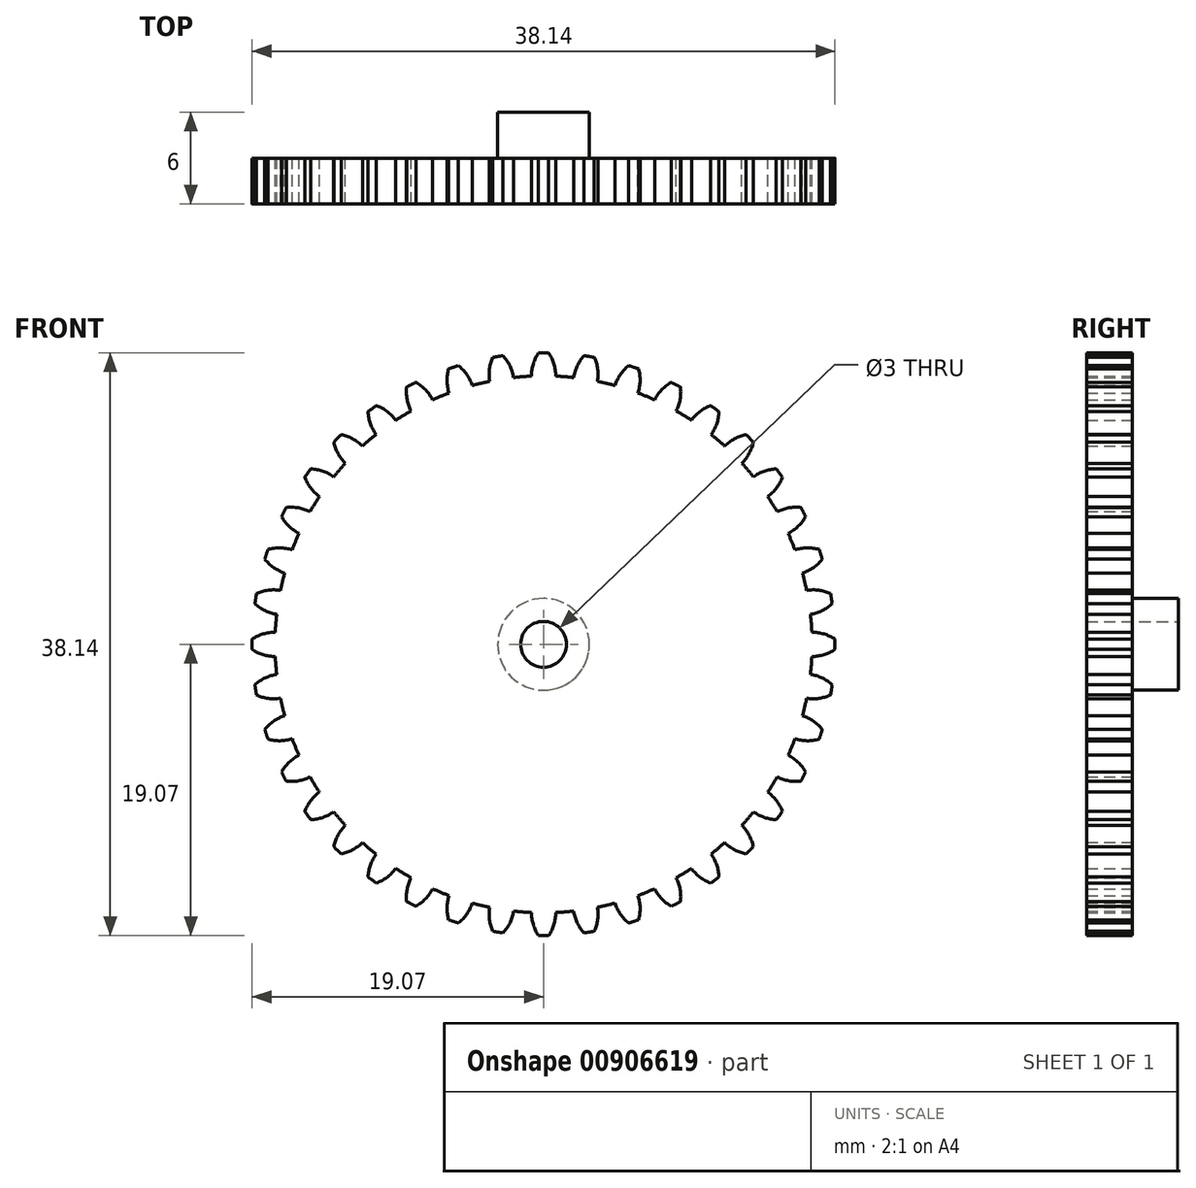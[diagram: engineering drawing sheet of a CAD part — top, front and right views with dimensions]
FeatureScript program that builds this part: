
annotation { "Feature Type Name" : "Feature", "Feature Type Description" : "" }
export const myFeature = defineFeature(function(context is Context, id is Id, definition is map)
    precondition{}
    {
        {
            var Q0;
            Q0=qCreatedBy(makeId("Front.planeOp"),FACE);
            var sketch = newSketch(context, id + "F0", { "sketchPlane" : qUnion([Q0])});
            skCircle(sketch, "E0", {"center": v(0, 0) * mm, "radius": 17.57 * mm});
            skArc(sketch, "E1", {"start": v(0.34, 19.07) * mm, "mid": v(0, 19.07) * mm, "end": v(-0.34, 19.07) * mm});
            skArc(sketch, "E2", {"start": v(-0.34, 19.07) * mm, "mid": v(-0.68, 18.34) * mm, "end": v(-0.8, 17.55) * mm});
            skArc(sketch, "E3.MirrorCS", {"start": v(0.34, 19.07) * mm, "mid": v(0.68, 18.34) * mm, "end": v(0.8, 17.55) * mm});
            skArc(sketch, "E4.1.0", {"start": v(-2.65, 18.89) * mm, "mid": v(-2.2, 18.22) * mm, "end": v(-1.96, 17.46) * mm});
            skArc(sketch, "E4.1.1", {"start": v(-2.65, 18.89) * mm, "mid": v(-2.98, 18.84) * mm, "end": v(-3.32, 18.78) * mm});
            skArc(sketch, "E4.1.2", {"start": v(-3.32, 18.78) * mm, "mid": v(-3.54, 18.01) * mm, "end": v(-3.53, 17.21) * mm});
            skArc(sketch, "E4.2.0", {"start": v(-5.57, 18.24) * mm, "mid": v(-5.02, 17.65) * mm, "end": v(-4.67, 16.94) * mm});
            skArc(sketch, "E4.2.1", {"start": v(-5.57, 18.24) * mm, "mid": v(-5.9, 18.14) * mm, "end": v(-6.21, 18.03) * mm});
            skArc(sketch, "E4.2.2", {"start": v(-6.21, 18.03) * mm, "mid": v(-6.31, 17.24) * mm, "end": v(-6.18, 16.45) * mm});
            skArc(sketch, "E4.3.0", {"start": v(-8.36, 17.14) * mm, "mid": v(-7.72, 16.65) * mm, "end": v(-7.26, 16) * mm});
            skArc(sketch, "E4.3.1", {"start": v(-8.36, 17.14) * mm, "mid": v(-8.66, 17) * mm, "end": v(-8.96, 16.84) * mm});
            skArc(sketch, "E4.3.2", {"start": v(-8.96, 16.84) * mm, "mid": v(-8.93, 16.04) * mm, "end": v(-8.68, 15.28) * mm});
            skArc(sketch, "E4.4.0", {"start": v(-10.93, 15.62) * mm, "mid": v(-10.23, 15.24) * mm, "end": v(-9.67, 14.67) * mm});
            skArc(sketch, "E4.4.1", {"start": v(-10.93, 15.62) * mm, "mid": v(-11.2, 15.43) * mm, "end": v(-11.48, 15.23) * mm});
            skArc(sketch, "E4.4.2", {"start": v(-11.48, 15.23) * mm, "mid": v(-11.33, 14.44) * mm, "end": v(-10.96, 13.73) * mm});
            skArc(sketch, "E4.5.0", {"start": v(-13.24, 13.72) * mm, "mid": v(-12.5, 13.45) * mm, "end": v(-11.85, 12.97) * mm});
            skArc(sketch, "E4.5.1", {"start": v(-13.24, 13.72) * mm, "mid": v(-13.48, 13.48) * mm, "end": v(-13.72, 13.24) * mm});
            skArc(sketch, "E4.5.2", {"start": v(-13.72, 13.24) * mm, "mid": v(-13.45, 12.5) * mm, "end": v(-12.97, 11.85) * mm});
            skArc(sketch, "E4.6.0", {"start": v(-15.23, 11.48) * mm, "mid": v(-14.44, 11.33) * mm, "end": v(-13.73, 10.96) * mm});
            skArc(sketch, "E4.6.1", {"start": v(-15.23, 11.48) * mm, "mid": v(-15.43, 11.2) * mm, "end": v(-15.62, 10.93) * mm});
            skArc(sketch, "E4.6.2", {"start": v(-15.62, 10.93) * mm, "mid": v(-15.24, 10.23) * mm, "end": v(-14.67, 9.67) * mm});
            skArc(sketch, "E4.7.0", {"start": v(-16.84, 8.96) * mm, "mid": v(-16.04, 8.93) * mm, "end": v(-15.28, 8.68) * mm});
            skArc(sketch, "E4.7.1", {"start": v(-16.84, 8.96) * mm, "mid": v(-17, 8.66) * mm, "end": v(-17.14, 8.36) * mm});
            skArc(sketch, "E4.7.2", {"start": v(-17.14, 8.36) * mm, "mid": v(-16.65, 7.72) * mm, "end": v(-16, 7.26) * mm});
            skArc(sketch, "E4.8.0", {"start": v(-18.03, 6.21) * mm, "mid": v(-17.24, 6.31) * mm, "end": v(-16.45, 6.18) * mm});
            skArc(sketch, "E4.8.1", {"start": v(-18.03, 6.21) * mm, "mid": v(-18.14, 5.9) * mm, "end": v(-18.24, 5.57) * mm});
            skArc(sketch, "E4.8.2", {"start": v(-18.24, 5.57) * mm, "mid": v(-17.65, 5.02) * mm, "end": v(-16.94, 4.67) * mm});
            skArc(sketch, "E5.1.9.0", {"start": v(-18.78, 3.32) * mm, "mid": v(-18.01, 3.54) * mm, "end": v(-17.21, 3.53) * mm});
            skArc(sketch, "E5.4.9.0", {"start": v(-18.78, 3.32) * mm, "mid": v(-18.84, 2.98) * mm, "end": v(-18.89, 2.65) * mm});
            skArc(sketch, "E5.8.9.0", {"start": v(-18.89, 2.65) * mm, "mid": v(-18.22, 2.2) * mm, "end": v(-17.46, 1.96) * mm});
            skArc(sketch, "E5.1.10.0", {"start": v(-19.07, 0.34) * mm, "mid": v(-18.34, 0.68) * mm, "end": v(-17.55, 0.8) * mm});
            skArc(sketch, "E5.4.10.0", {"start": v(-19.07, 0.34) * mm, "mid": v(-19.07, 0) * mm, "end": v(-19.07, -0.34) * mm});
            skArc(sketch, "E5.8.10.0", {"start": v(-19.07, -0.34) * mm, "mid": v(-18.34, -0.68) * mm, "end": v(-17.55, -0.8) * mm});
            skArc(sketch, "E5.1.11.0", {"start": v(-18.89, -2.65) * mm, "mid": v(-18.22, -2.2) * mm, "end": v(-17.46, -1.96) * mm});
            skArc(sketch, "E5.4.11.0", {"start": v(-18.89, -2.65) * mm, "mid": v(-18.84, -2.98) * mm, "end": v(-18.78, -3.32) * mm});
            skArc(sketch, "E5.8.11.0", {"start": v(-18.78, -3.32) * mm, "mid": v(-18.01, -3.54) * mm, "end": v(-17.21, -3.53) * mm});
            skArc(sketch, "E5.1.12.0", {"start": v(-18.24, -5.57) * mm, "mid": v(-17.65, -5.02) * mm, "end": v(-16.94, -4.67) * mm});
            skArc(sketch, "E5.4.12.0", {"start": v(-18.24, -5.57) * mm, "mid": v(-18.14, -5.9) * mm, "end": v(-18.03, -6.21) * mm});
            skArc(sketch, "E5.8.12.0", {"start": v(-18.03, -6.21) * mm, "mid": v(-17.24, -6.31) * mm, "end": v(-16.45, -6.18) * mm});
            skArc(sketch, "E5.1.13.0", {"start": v(-17.14, -8.36) * mm, "mid": v(-16.65, -7.72) * mm, "end": v(-16, -7.26) * mm});
            skArc(sketch, "E5.4.13.0", {"start": v(-17.14, -8.36) * mm, "mid": v(-17, -8.66) * mm, "end": v(-16.84, -8.96) * mm});
            skArc(sketch, "E5.8.13.0", {"start": v(-16.84, -8.96) * mm, "mid": v(-16.04, -8.93) * mm, "end": v(-15.28, -8.68) * mm});
            skArc(sketch, "E5.1.14.0", {"start": v(-15.62, -10.93) * mm, "mid": v(-15.24, -10.23) * mm, "end": v(-14.67, -9.67) * mm});
            skArc(sketch, "E5.4.14.0", {"start": v(-15.62, -10.93) * mm, "mid": v(-15.43, -11.2) * mm, "end": v(-15.23, -11.48) * mm});
            skArc(sketch, "E5.8.14.0", {"start": v(-15.23, -11.48) * mm, "mid": v(-14.44, -11.33) * mm, "end": v(-13.73, -10.96) * mm});
            skArc(sketch, "E5.1.15.0", {"start": v(-13.72, -13.24) * mm, "mid": v(-13.45, -12.5) * mm, "end": v(-12.97, -11.85) * mm});
            skArc(sketch, "E5.4.15.0", {"start": v(-13.72, -13.24) * mm, "mid": v(-13.48, -13.48) * mm, "end": v(-13.24, -13.72) * mm});
            skArc(sketch, "E5.8.15.0", {"start": v(-13.24, -13.72) * mm, "mid": v(-12.5, -13.45) * mm, "end": v(-11.85, -12.97) * mm});
            skArc(sketch, "E5.1.16.0", {"start": v(-11.48, -15.23) * mm, "mid": v(-11.33, -14.44) * mm, "end": v(-10.96, -13.73) * mm});
            skArc(sketch, "E5.4.16.0", {"start": v(-11.48, -15.23) * mm, "mid": v(-11.2, -15.43) * mm, "end": v(-10.93, -15.62) * mm});
            skArc(sketch, "E5.8.16.0", {"start": v(-10.93, -15.62) * mm, "mid": v(-10.23, -15.24) * mm, "end": v(-9.67, -14.67) * mm});
            skArc(sketch, "E5.1.17.0", {"start": v(-8.96, -16.84) * mm, "mid": v(-8.93, -16.04) * mm, "end": v(-8.68, -15.28) * mm});
            skArc(sketch, "E5.4.17.0", {"start": v(-8.96, -16.84) * mm, "mid": v(-8.66, -17) * mm, "end": v(-8.36, -17.14) * mm});
            skArc(sketch, "E5.8.17.0", {"start": v(-8.36, -17.14) * mm, "mid": v(-7.72, -16.65) * mm, "end": v(-7.26, -16) * mm});
            skArc(sketch, "E6.1.18.0", {"start": v(-6.21, -18.03) * mm, "mid": v(-6.31, -17.24) * mm, "end": v(-6.18, -16.45) * mm});
            skArc(sketch, "E6.4.18.0", {"start": v(-6.21, -18.03) * mm, "mid": v(-5.9, -18.14) * mm, "end": v(-5.57, -18.24) * mm});
            skArc(sketch, "E6.8.18.0", {"start": v(-5.57, -18.24) * mm, "mid": v(-5.02, -17.65) * mm, "end": v(-4.67, -16.94) * mm});
            skArc(sketch, "E7.1.19.0", {"start": v(-3.32, -18.78) * mm, "mid": v(-3.54, -18.01) * mm, "end": v(-3.53, -17.21) * mm});
            skArc(sketch, "E7.4.19.0", {"start": v(-3.32, -18.78) * mm, "mid": v(-2.98, -18.84) * mm, "end": v(-2.65, -18.89) * mm});
            skArc(sketch, "E7.8.19.0", {"start": v(-2.65, -18.89) * mm, "mid": v(-2.2, -18.22) * mm, "end": v(-1.96, -17.46) * mm});
            skArc(sketch, "E8.1.20.0", {"start": v(-0.34, -19.07) * mm, "mid": v(-0.68, -18.34) * mm, "end": v(-0.8, -17.55) * mm});
            skArc(sketch, "E8.4.20.0", {"start": v(-0.34, -19.07) * mm, "mid": v(0, -19.07) * mm, "end": v(0.34, -19.07) * mm});
            skArc(sketch, "E8.8.20.0", {"start": v(0.34, -19.07) * mm, "mid": v(0.68, -18.34) * mm, "end": v(0.8, -17.55) * mm});
            skArc(sketch, "E8.1.21.0", {"start": v(2.65, -18.89) * mm, "mid": v(2.2, -18.22) * mm, "end": v(1.96, -17.46) * mm});
            skArc(sketch, "E8.4.21.0", {"start": v(2.65, -18.89) * mm, "mid": v(2.98, -18.84) * mm, "end": v(3.32, -18.78) * mm});
            skArc(sketch, "E8.8.21.0", {"start": v(3.32, -18.78) * mm, "mid": v(3.54, -18.01) * mm, "end": v(3.53, -17.21) * mm});
            skArc(sketch, "E8.1.22.0", {"start": v(5.57, -18.24) * mm, "mid": v(5.02, -17.65) * mm, "end": v(4.67, -16.94) * mm});
            skArc(sketch, "E8.4.22.0", {"start": v(5.57, -18.24) * mm, "mid": v(5.9, -18.14) * mm, "end": v(6.21, -18.03) * mm});
            skArc(sketch, "E8.8.22.0", {"start": v(6.21, -18.03) * mm, "mid": v(6.31, -17.24) * mm, "end": v(6.18, -16.45) * mm});
            skArc(sketch, "E8.1.23.0", {"start": v(8.36, -17.14) * mm, "mid": v(7.72, -16.65) * mm, "end": v(7.26, -16) * mm});
            skArc(sketch, "E8.4.23.0", {"start": v(8.36, -17.14) * mm, "mid": v(8.66, -17) * mm, "end": v(8.96, -16.84) * mm});
            skArc(sketch, "E8.8.23.0", {"start": v(8.96, -16.84) * mm, "mid": v(8.93, -16.04) * mm, "end": v(8.68, -15.28) * mm});
            skArc(sketch, "E8.1.24.0", {"start": v(10.93, -15.62) * mm, "mid": v(10.23, -15.24) * mm, "end": v(9.67, -14.67) * mm});
            skArc(sketch, "E8.4.24.0", {"start": v(10.93, -15.62) * mm, "mid": v(11.2, -15.43) * mm, "end": v(11.48, -15.23) * mm});
            skArc(sketch, "E8.8.24.0", {"start": v(11.48, -15.23) * mm, "mid": v(11.33, -14.44) * mm, "end": v(10.96, -13.73) * mm});
            skArc(sketch, "E8.1.25.0", {"start": v(13.24, -13.72) * mm, "mid": v(12.5, -13.45) * mm, "end": v(11.85, -12.97) * mm});
            skArc(sketch, "E8.4.25.0", {"start": v(13.24, -13.72) * mm, "mid": v(13.48, -13.48) * mm, "end": v(13.72, -13.24) * mm});
            skArc(sketch, "E8.8.25.0", {"start": v(13.72, -13.24) * mm, "mid": v(13.45, -12.5) * mm, "end": v(12.97, -11.85) * mm});
            skArc(sketch, "E8.1.26.0", {"start": v(15.23, -11.48) * mm, "mid": v(14.44, -11.33) * mm, "end": v(13.73, -10.96) * mm});
            skArc(sketch, "E8.4.26.0", {"start": v(15.23, -11.48) * mm, "mid": v(15.43, -11.2) * mm, "end": v(15.62, -10.93) * mm});
            skArc(sketch, "E8.8.26.0", {"start": v(15.62, -10.93) * mm, "mid": v(15.24, -10.23) * mm, "end": v(14.67, -9.67) * mm});
            skArc(sketch, "E8.1.27.0", {"start": v(16.84, -8.96) * mm, "mid": v(16.04, -8.93) * mm, "end": v(15.28, -8.68) * mm});
            skArc(sketch, "E8.4.27.0", {"start": v(16.84, -8.96) * mm, "mid": v(17, -8.66) * mm, "end": v(17.14, -8.36) * mm});
            skArc(sketch, "E8.8.27.0", {"start": v(17.14, -8.36) * mm, "mid": v(16.65, -7.72) * mm, "end": v(16, -7.26) * mm});
            skArc(sketch, "E8.1.28.0", {"start": v(18.03, -6.21) * mm, "mid": v(17.24, -6.31) * mm, "end": v(16.45, -6.18) * mm});
            skArc(sketch, "E8.4.28.0", {"start": v(18.03, -6.21) * mm, "mid": v(18.14, -5.9) * mm, "end": v(18.24, -5.57) * mm});
            skArc(sketch, "E8.8.28.0", {"start": v(18.24, -5.57) * mm, "mid": v(17.65, -5.02) * mm, "end": v(16.94, -4.67) * mm});
            skArc(sketch, "E8.1.29.0", {"start": v(18.78, -3.32) * mm, "mid": v(18.01, -3.54) * mm, "end": v(17.21, -3.53) * mm});
            skArc(sketch, "E8.4.29.0", {"start": v(18.78, -3.32) * mm, "mid": v(18.84, -2.98) * mm, "end": v(18.89, -2.65) * mm});
            skArc(sketch, "E8.8.29.0", {"start": v(18.89, -2.65) * mm, "mid": v(18.22, -2.2) * mm, "end": v(17.46, -1.96) * mm});
            skArc(sketch, "E9.1.30.0", {"start": v(19.07, -0.34) * mm, "mid": v(18.34, -0.68) * mm, "end": v(17.55, -0.8) * mm});
            skArc(sketch, "E9.4.30.0", {"start": v(19.07, -0.34) * mm, "mid": v(19.07, 0) * mm, "end": v(19.07, 0.34) * mm});
            skArc(sketch, "E9.8.30.0", {"start": v(19.07, 0.34) * mm, "mid": v(18.34, 0.68) * mm, "end": v(17.55, 0.8) * mm});
            skArc(sketch, "E9.1.31.0", {"start": v(18.89, 2.65) * mm, "mid": v(18.22, 2.2) * mm, "end": v(17.46, 1.96) * mm});
            skArc(sketch, "E9.4.31.0", {"start": v(18.89, 2.65) * mm, "mid": v(18.84, 2.98) * mm, "end": v(18.78, 3.32) * mm});
            skArc(sketch, "E9.8.31.0", {"start": v(18.78, 3.32) * mm, "mid": v(18.01, 3.54) * mm, "end": v(17.21, 3.53) * mm});
            skArc(sketch, "E9.1.32.0", {"start": v(18.24, 5.57) * mm, "mid": v(17.65, 5.02) * mm, "end": v(16.94, 4.67) * mm});
            skArc(sketch, "E9.4.32.0", {"start": v(18.24, 5.57) * mm, "mid": v(18.14, 5.9) * mm, "end": v(18.03, 6.21) * mm});
            skArc(sketch, "E9.8.32.0", {"start": v(18.03, 6.21) * mm, "mid": v(17.24, 6.31) * mm, "end": v(16.45, 6.18) * mm});
            skArc(sketch, "E9.1.33.0", {"start": v(17.14, 8.36) * mm, "mid": v(16.65, 7.72) * mm, "end": v(16, 7.26) * mm});
            skArc(sketch, "E9.4.33.0", {"start": v(17.14, 8.36) * mm, "mid": v(17, 8.66) * mm, "end": v(16.84, 8.96) * mm});
            skArc(sketch, "E9.8.33.0", {"start": v(16.84, 8.96) * mm, "mid": v(16.04, 8.93) * mm, "end": v(15.28, 8.68) * mm});
            skArc(sketch, "E9.1.34.0", {"start": v(15.62, 10.93) * mm, "mid": v(15.24, 10.23) * mm, "end": v(14.67, 9.67) * mm});
            skArc(sketch, "E9.4.34.0", {"start": v(15.62, 10.93) * mm, "mid": v(15.43, 11.2) * mm, "end": v(15.23, 11.48) * mm});
            skArc(sketch, "E9.8.34.0", {"start": v(15.23, 11.48) * mm, "mid": v(14.44, 11.33) * mm, "end": v(13.73, 10.96) * mm});
            skArc(sketch, "E9.1.35.0", {"start": v(13.72, 13.24) * mm, "mid": v(13.45, 12.5) * mm, "end": v(12.97, 11.85) * mm});
            skArc(sketch, "E9.4.35.0", {"start": v(13.72, 13.24) * mm, "mid": v(13.48, 13.48) * mm, "end": v(13.24, 13.72) * mm});
            skArc(sketch, "E9.8.35.0", {"start": v(13.24, 13.72) * mm, "mid": v(12.5, 13.45) * mm, "end": v(11.85, 12.97) * mm});
            skArc(sketch, "E9.1.36.0", {"start": v(11.48, 15.23) * mm, "mid": v(11.33, 14.44) * mm, "end": v(10.96, 13.73) * mm});
            skArc(sketch, "E9.4.36.0", {"start": v(11.48, 15.23) * mm, "mid": v(11.2, 15.43) * mm, "end": v(10.93, 15.62) * mm});
            skArc(sketch, "E9.8.36.0", {"start": v(10.93, 15.62) * mm, "mid": v(10.23, 15.24) * mm, "end": v(9.67, 14.67) * mm});
            skArc(sketch, "E9.1.37.0", {"start": v(8.96, 16.84) * mm, "mid": v(8.93, 16.04) * mm, "end": v(8.68, 15.28) * mm});
            skArc(sketch, "E9.4.37.0", {"start": v(8.96, 16.84) * mm, "mid": v(8.66, 17) * mm, "end": v(8.36, 17.14) * mm});
            skArc(sketch, "E9.8.37.0", {"start": v(8.36, 17.14) * mm, "mid": v(7.72, 16.65) * mm, "end": v(7.26, 16) * mm});
            skArc(sketch, "E9.1.38.0", {"start": v(6.21, 18.03) * mm, "mid": v(6.31, 17.24) * mm, "end": v(6.18, 16.45) * mm});
            skArc(sketch, "E9.4.38.0", {"start": v(6.21, 18.03) * mm, "mid": v(5.9, 18.14) * mm, "end": v(5.57, 18.24) * mm});
            skArc(sketch, "E9.8.38.0", {"start": v(5.57, 18.24) * mm, "mid": v(5.02, 17.65) * mm, "end": v(4.67, 16.94) * mm});
            skArc(sketch, "E9.1.39.0", {"start": v(3.32, 18.78) * mm, "mid": v(3.54, 18.01) * mm, "end": v(3.53, 17.21) * mm});
            skArc(sketch, "E9.4.39.0", {"start": v(3.32, 18.78) * mm, "mid": v(2.98, 18.84) * mm, "end": v(2.65, 18.89) * mm});
            skArc(sketch, "E9.8.39.0", {"start": v(2.65, 18.89) * mm, "mid": v(2.2, 18.22) * mm, "end": v(1.96, 17.46) * mm});
            skSolve(sketch);
        }
        {
            var Q0;
            Q0=qSketchRegion(id+"F0",true);
            extrude(context, id + "F1", {"entities" : qUnion([Q0]), "depth" : 3 * mm, "offsetDistance" : 25 * mm});
        }
        {
            var Q0;
            Q0=makeQuery(id+"F1.opExtrude","CAP_FACE",FACE,{"disambiguationData":[OSD([sQuery(id+"F0.wireOp",EDGE,"E0"),sQuery(id+"F0.wireOp",EDGE,"E1"),sQuery(id+"F0.wireOp",EDGE,"E2"),sQuery(id+"F0.wireOp",EDGE,"E3.MirrorCS"),sQuery(id+"F0.wireOp",EDGE,"E4.1.0"),sQuery(id+"F0.wireOp",EDGE,"E4.1.1"),sQuery(id+"F0.wireOp",EDGE,"E4.1.2"),sQuery(id+"F0.wireOp",EDGE,"E4.2.0"),sQuery(id+"F0.wireOp",EDGE,"E4.2.1"),sQuery(id+"F0.wireOp",EDGE,"E4.2.2"),sQuery(id+"F0.wireOp",EDGE,"E4.3.0"),sQuery(id+"F0.wireOp",EDGE,"E4.3.1"),sQuery(id+"F0.wireOp",EDGE,"E4.3.2"),sQuery(id+"F0.wireOp",EDGE,"E4.4.0"),sQuery(id+"F0.wireOp",EDGE,"E4.4.1"),sQuery(id+"F0.wireOp",EDGE,"E4.4.2"),sQuery(id+"F0.wireOp",EDGE,"E4.5.0"),sQuery(id+"F0.wireOp",EDGE,"E4.5.1"),sQuery(id+"F0.wireOp",EDGE,"E4.5.2"),sQuery(id+"F0.wireOp",EDGE,"E4.6.0"),sQuery(id+"F0.wireOp",EDGE,"E4.6.1"),sQuery(id+"F0.wireOp",EDGE,"E4.6.2"),sQuery(id+"F0.wireOp",EDGE,"E4.7.0"),sQuery(id+"F0.wireOp",EDGE,"E4.7.1"),sQuery(id+"F0.wireOp",EDGE,"E4.7.2"),sQuery(id+"F0.wireOp",EDGE,"E4.8.0"),sQuery(id+"F0.wireOp",EDGE,"E4.8.1"),sQuery(id+"F0.wireOp",EDGE,"E4.8.2")])],"isStart":true});
            var sketch = newSketch(context, id + "F2", { "sketchPlane" : qUnion([Q0])});
            skCircle(sketch, "E10", {"center": v(0, 0) * mm, "radius": 1.5 * mm});
            skSolve(sketch);
        }
        {
            var Q0;
            Q0=makeQuery(id+"F2.imprint","IMPRINT",FACE,{"disambiguationData":[TD([[makeQuery(id+"F2.imprint","IMPRINT",EDGE,{"derivedFrom":sQuery(id+"F2.wireOp",EDGE,"E10")}),1.0]])]});
            extrude(context, id + "F3", {"entities" : qUnion([Q0]), "operationType" : NewBodyOperationType.REMOVE, "endBound" : BoundingType.THROUGH_ALL, "oppositeDirection" : true, "depth" : 25 * mm, "offsetDistance" : 25 * mm});
        }
        {
            var Q0;
            Q0=makeQuery(id+"F1.opExtrude","CAP_FACE",FACE,{"disambiguationData":[OSD([sQuery(id+"F0.wireOp",EDGE,"E0"),sQuery(id+"F0.wireOp",EDGE,"E1"),sQuery(id+"F0.wireOp",EDGE,"E2"),sQuery(id+"F0.wireOp",EDGE,"E3.MirrorCS"),sQuery(id+"F0.wireOp",EDGE,"E4.1.0"),sQuery(id+"F0.wireOp",EDGE,"E4.1.1"),sQuery(id+"F0.wireOp",EDGE,"E4.1.2"),sQuery(id+"F0.wireOp",EDGE,"E4.2.0"),sQuery(id+"F0.wireOp",EDGE,"E4.2.1"),sQuery(id+"F0.wireOp",EDGE,"E4.2.2"),sQuery(id+"F0.wireOp",EDGE,"E4.3.0"),sQuery(id+"F0.wireOp",EDGE,"E4.3.1"),sQuery(id+"F0.wireOp",EDGE,"E4.3.2"),sQuery(id+"F0.wireOp",EDGE,"E4.4.0"),sQuery(id+"F0.wireOp",EDGE,"E4.4.1"),sQuery(id+"F0.wireOp",EDGE,"E4.4.2"),sQuery(id+"F0.wireOp",EDGE,"E4.5.0"),sQuery(id+"F0.wireOp",EDGE,"E4.5.1"),sQuery(id+"F0.wireOp",EDGE,"E4.5.2"),sQuery(id+"F0.wireOp",EDGE,"E4.6.0"),sQuery(id+"F0.wireOp",EDGE,"E4.6.1"),sQuery(id+"F0.wireOp",EDGE,"E4.6.2"),sQuery(id+"F0.wireOp",EDGE,"E4.7.0"),sQuery(id+"F0.wireOp",EDGE,"E4.7.1"),sQuery(id+"F0.wireOp",EDGE,"E4.7.2"),sQuery(id+"F0.wireOp",EDGE,"E4.8.0"),sQuery(id+"F0.wireOp",EDGE,"E4.8.1"),sQuery(id+"F0.wireOp",EDGE,"E4.8.2"),sQuery(id+"F0.wireOp",EDGE,"E5.1.9.0"),sQuery(id+"F0.wireOp",EDGE,"E5.4.9.0"),sQuery(id+"F0.wireOp",EDGE,"E5.8.9.0"),sQuery(id+"F0.wireOp",EDGE,"E5.1.10.0"),sQuery(id+"F0.wireOp",EDGE,"E5.4.10.0"),sQuery(id+"F0.wireOp",EDGE,"E5.8.10.0"),sQuery(id+"F0.wireOp",EDGE,"E5.1.11.0"),sQuery(id+"F0.wireOp",EDGE,"E5.4.11.0"),sQuery(id+"F0.wireOp",EDGE,"E5.8.11.0"),sQuery(id+"F0.wireOp",EDGE,"E5.1.12.0"),sQuery(id+"F0.wireOp",EDGE,"E5.4.12.0"),sQuery(id+"F0.wireOp",EDGE,"E5.8.12.0"),sQuery(id+"F0.wireOp",EDGE,"E5.1.13.0"),sQuery(id+"F0.wireOp",EDGE,"E5.4.13.0"),sQuery(id+"F0.wireOp",EDGE,"E5.8.13.0"),sQuery(id+"F0.wireOp",EDGE,"E5.1.14.0"),sQuery(id+"F0.wireOp",EDGE,"E5.4.14.0"),sQuery(id+"F0.wireOp",EDGE,"E5.8.14.0"),sQuery(id+"F0.wireOp",EDGE,"E5.1.15.0"),sQuery(id+"F0.wireOp",EDGE,"E5.4.15.0"),sQuery(id+"F0.wireOp",EDGE,"E5.8.15.0"),sQuery(id+"F0.wireOp",EDGE,"E5.1.16.0"),sQuery(id+"F0.wireOp",EDGE,"E5.4.16.0"),sQuery(id+"F0.wireOp",EDGE,"E5.8.16.0"),sQuery(id+"F0.wireOp",EDGE,"E5.1.17.0"),sQuery(id+"F0.wireOp",EDGE,"E5.4.17.0"),sQuery(id+"F0.wireOp",EDGE,"E5.8.17.0"),sQuery(id+"F0.wireOp",EDGE,"E6.1.18.0"),sQuery(id+"F0.wireOp",EDGE,"E6.4.18.0"),sQuery(id+"F0.wireOp",EDGE,"E6.8.18.0"),sQuery(id+"F0.wireOp",EDGE,"E7.1.19.0"),sQuery(id+"F0.wireOp",EDGE,"E7.4.19.0"),sQuery(id+"F0.wireOp",EDGE,"E7.8.19.0"),sQuery(id+"F0.wireOp",EDGE,"E8.1.20.0"),sQuery(id+"F0.wireOp",EDGE,"E8.4.20.0"),sQuery(id+"F0.wireOp",EDGE,"E8.8.20.0"),sQuery(id+"F0.wireOp",EDGE,"E8.1.21.0"),sQuery(id+"F0.wireOp",EDGE,"E8.4.21.0"),sQuery(id+"F0.wireOp",EDGE,"E8.8.21.0"),sQuery(id+"F0.wireOp",EDGE,"E8.1.22.0"),sQuery(id+"F0.wireOp",EDGE,"E8.4.22.0"),sQuery(id+"F0.wireOp",EDGE,"E8.8.22.0"),sQuery(id+"F0.wireOp",EDGE,"E8.1.23.0"),sQuery(id+"F0.wireOp",EDGE,"E8.4.23.0"),sQuery(id+"F0.wireOp",EDGE,"E8.8.23.0"),sQuery(id+"F0.wireOp",EDGE,"E8.1.24.0"),sQuery(id+"F0.wireOp",EDGE,"E8.4.24.0"),sQuery(id+"F0.wireOp",EDGE,"E8.8.24.0"),sQuery(id+"F0.wireOp",EDGE,"E8.1.25.0"),sQuery(id+"F0.wireOp",EDGE,"E8.4.25.0"),sQuery(id+"F0.wireOp",EDGE,"E8.8.25.0"),sQuery(id+"F0.wireOp",EDGE,"E8.1.26.0"),sQuery(id+"F0.wireOp",EDGE,"E8.4.26.0"),sQuery(id+"F0.wireOp",EDGE,"E8.8.26.0"),sQuery(id+"F0.wireOp",EDGE,"E8.1.27.0"),sQuery(id+"F0.wireOp",EDGE,"E8.4.27.0"),sQuery(id+"F0.wireOp",EDGE,"E8.8.27.0"),sQuery(id+"F0.wireOp",EDGE,"E8.1.28.0"),sQuery(id+"F0.wireOp",EDGE,"E8.4.28.0"),sQuery(id+"F0.wireOp",EDGE,"E8.8.28.0"),sQuery(id+"F0.wireOp",EDGE,"E8.1.29.0"),sQuery(id+"F0.wireOp",EDGE,"E8.4.29.0"),sQuery(id+"F0.wireOp",EDGE,"E8.8.29.0"),sQuery(id+"F0.wireOp",EDGE,"E9.1.30.0"),sQuery(id+"F0.wireOp",EDGE,"E9.4.30.0"),sQuery(id+"F0.wireOp",EDGE,"E9.8.30.0"),sQuery(id+"F0.wireOp",EDGE,"E9.1.31.0"),sQuery(id+"F0.wireOp",EDGE,"E9.4.31.0"),sQuery(id+"F0.wireOp",EDGE,"E9.8.31.0"),sQuery(id+"F0.wireOp",EDGE,"E9.1.32.0"),sQuery(id+"F0.wireOp",EDGE,"E9.4.32.0"),sQuery(id+"F0.wireOp",EDGE,"E9.8.32.0"),sQuery(id+"F0.wireOp",EDGE,"E9.1.33.0"),sQuery(id+"F0.wireOp",EDGE,"E9.4.33.0"),sQuery(id+"F0.wireOp",EDGE,"E9.8.33.0"),sQuery(id+"F0.wireOp",EDGE,"E9.1.34.0"),sQuery(id+"F0.wireOp",EDGE,"E9.4.34.0"),sQuery(id+"F0.wireOp",EDGE,"E9.8.34.0"),sQuery(id+"F0.wireOp",EDGE,"E9.1.35.0"),sQuery(id+"F0.wireOp",EDGE,"E9.4.35.0"),sQuery(id+"F0.wireOp",EDGE,"E9.8.35.0"),sQuery(id+"F0.wireOp",EDGE,"E9.1.36.0"),sQuery(id+"F0.wireOp",EDGE,"E9.4.36.0"),sQuery(id+"F0.wireOp",EDGE,"E9.8.36.0"),sQuery(id+"F0.wireOp",EDGE,"E9.1.37.0"),sQuery(id+"F0.wireOp",EDGE,"E9.4.37.0"),sQuery(id+"F0.wireOp",EDGE,"E9.8.37.0"),sQuery(id+"F0.wireOp",EDGE,"E9.1.38.0"),sQuery(id+"F0.wireOp",EDGE,"E9.4.38.0"),sQuery(id+"F0.wireOp",EDGE,"E9.8.38.0"),sQuery(id+"F0.wireOp",EDGE,"E9.1.39.0"),sQuery(id+"F0.wireOp",EDGE,"E9.4.39.0"),sQuery(id+"F0.wireOp",EDGE,"E9.8.39.0")])],"isStart":true});
            var sketch = newSketch(context, id + "F4", { "sketchPlane" : qUnion([Q0])});
            skCircle(sketch, "E11", {"center": v(0, 0) * mm, "radius": 3 * mm});
            skCircle(sketch, "E12.0", {"center": v(0, 0) * mm, "radius": 1.5 * mm});
            skSolve(sketch);
        }
        {
            var Q0;
            Q0 = qSketchRegion(id + "F4", true);
            extrude(context, id + "F5", {"entities" : qUnion([Q0]), "operationType" : NewBodyOperationType.ADD, "depth" : 3 * mm, "offsetDistance" : 25 * mm});
        }
    });
